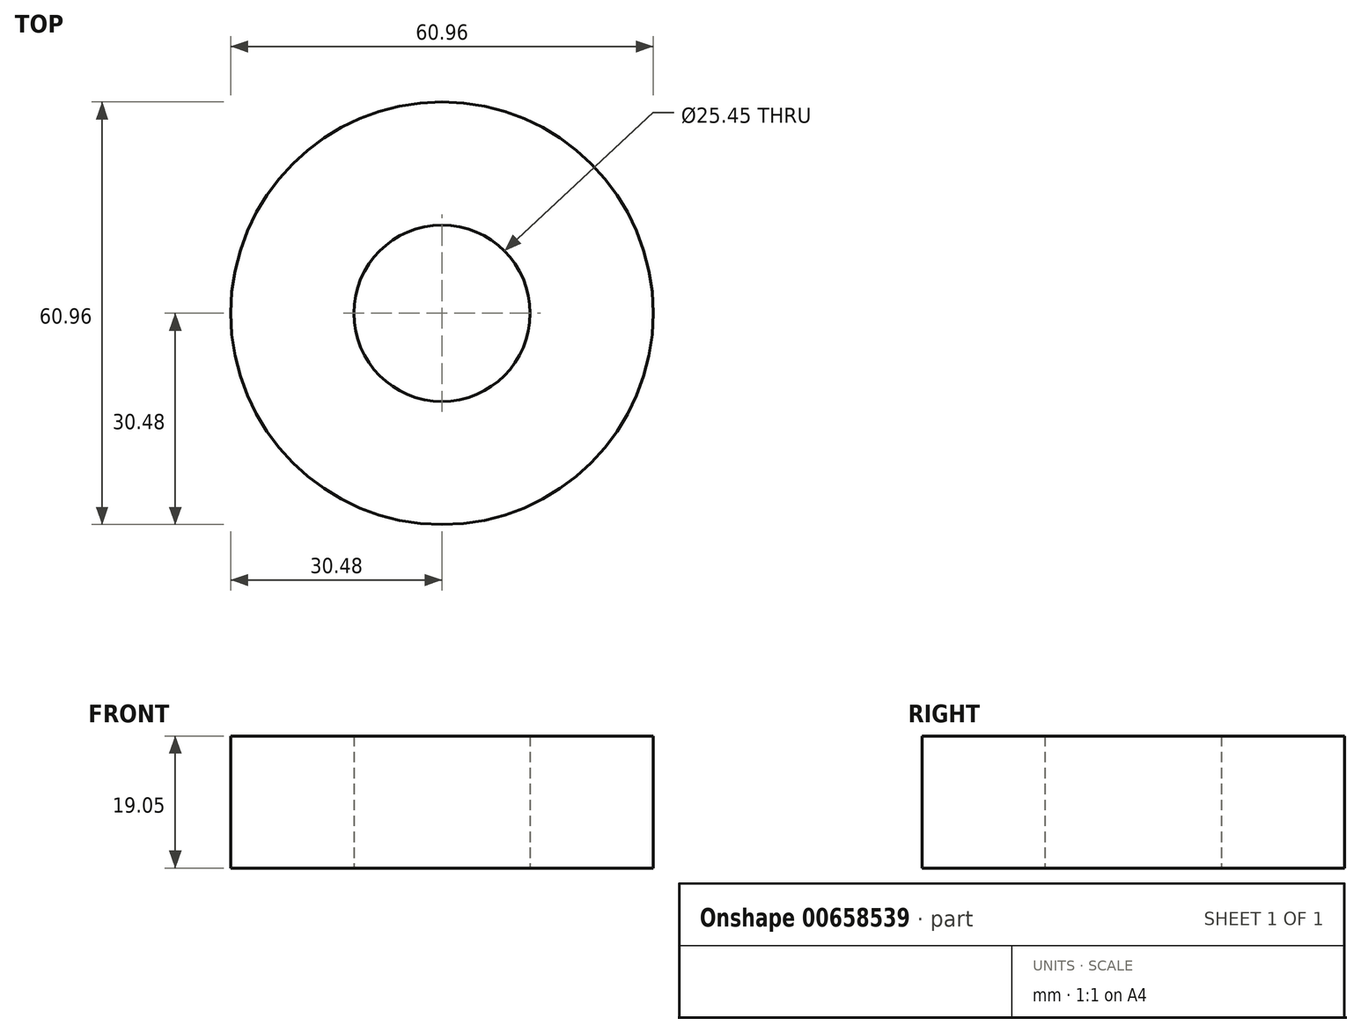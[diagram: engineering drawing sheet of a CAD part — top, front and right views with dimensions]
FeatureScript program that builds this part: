
annotation { "Feature Type Name" : "Feature", "Feature Type Description" : "" }
export const myFeature = defineFeature(function(context is Context, id is Id, definition is map)
    precondition{}
    {
        {
            var Q0;
            Q0=qCreatedBy(makeId("Front.planeOp"),FACE);
            var sketch = newSketch(context, id + "F0", { "sketchPlane" : qUnion([Q0])});
            skLineSegment(sketch, "E0", {"start": v(0, 0) * mm, "end": v(0, 34.25) * mm});
            skLineSegment(sketch, "E1", {"start": v(12.73, 0) * mm, "end": v(12.73, 19.05) * mm});
            skLineSegment(sketch, "E2", {"start": v(12.73, 19.05) * mm, "end": v(30.48, 19.05) * mm});
            skLineSegment(sketch, "E3", {"start": v(30.48, 19.05) * mm, "end": v(30.48, 0) * mm});
            skLineSegment(sketch, "E4", {"start": v(30.48, 0) * mm, "end": v(12.73, 0) * mm});
            skSolve(sketch);
        }
        {
            var Q0;
            Q0 = qSketchRegion(id + "F0", true);
            var Q1;
            Q1=sQuery(id+"F0.wireOp",EDGE,"E0");
            revolve(context, id + "F1", {"entities" : qUnion([Q0]), "axis" : qUnion([Q1]), "revolveType" : RevolveType.FULL});
        }
    });
